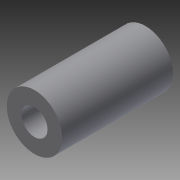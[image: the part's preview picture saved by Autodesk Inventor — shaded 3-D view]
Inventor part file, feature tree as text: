
AUTODESK INVENTOR PART (.ipt)
format: ipt  version: 2014 SP2 (Build 180246200, 246)  size: 98,816 bytes
history: native  units: in
note: dims shown in document units (in); Inventor stores cm internally (conversion verified against a paired STEP export)
features: other x7, sketch x2, revolve x1, hole x1
ambient origin geometry x8: Origin, YZ Plane, XZ Plane, XY Plane, X Axis, Y Axis, Z Axis, Center Point
bodies: Solid1 (feature_tree)
feature tree (11):
  revolve  "Revolution1"  [1 undecoded]
  hole  "Hole1"  [1 undecoded]
  other  "screw_XY"
  other  "screw_YZ"
  other  "screw_ZX"
  other  "screw_X"
  other  "screw_Y"
  other  "screw_Z"
  other  "screw_Center"
  sketch  "Sketch_1"  dims[d0=360.0deg]
  sketch  "Sketch2"  dims[d1=0.147in d2=0.75in d3=0.375in d4=0.25in d5=0.5635in d6=0.625in d7=0.0in d8=0.0in]
note: 2 required parameter values undecoded (feature->parameter linkage not recoverable at this tier; creation-order binding heuristic only, values carry confidence <= 0.55)